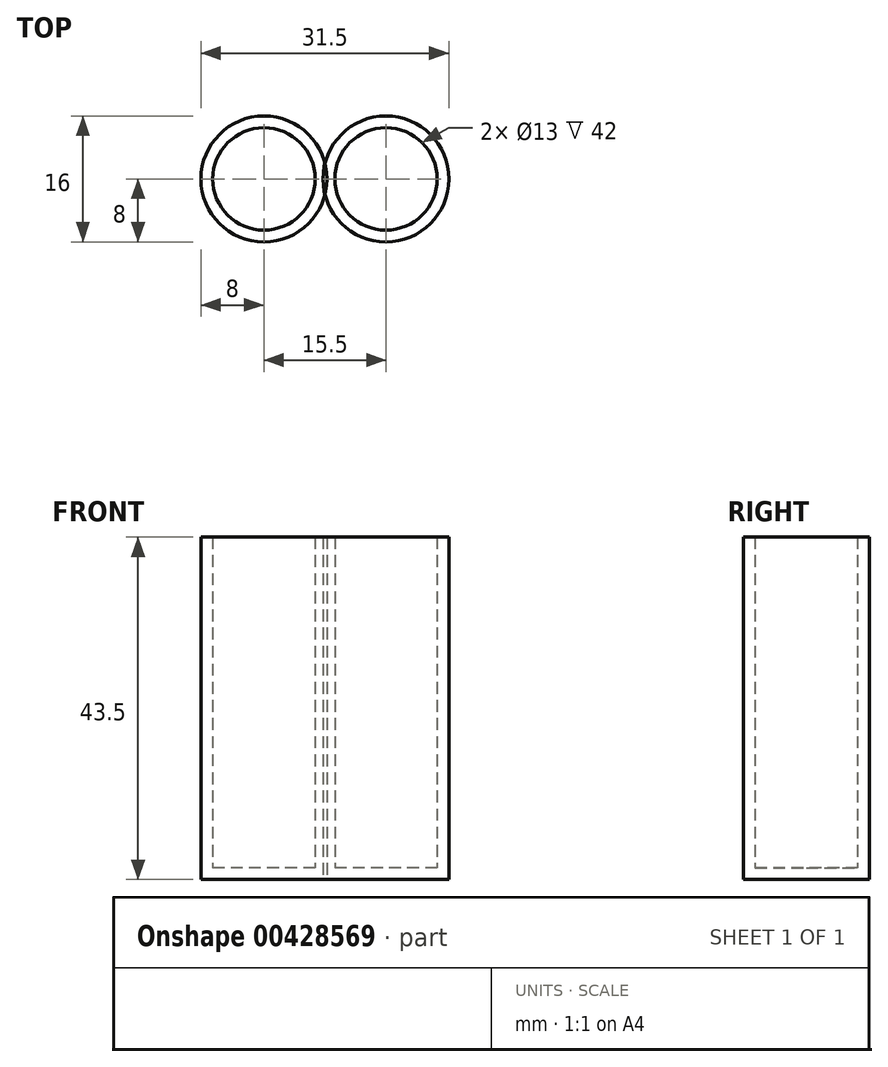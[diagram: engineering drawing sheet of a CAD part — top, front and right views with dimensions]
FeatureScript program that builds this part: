
annotation { "Feature Type Name" : "Feature", "Feature Type Description" : "" }
export const myFeature = defineFeature(function(context is Context, id is Id, definition is map)
    precondition{}
    {
        {
            var Q0;
            Q0=qCreatedBy(makeId("Top.planeOp"),FACE);
            var sketch = newSketch(context, id + "F0", { "sketchPlane" : qUnion([Q0])});
            skCircle(sketch, "E0", {"center": v(0, 0) * mm, "radius": 8 * mm});
            skSolve(sketch);
        }
        {
            var Q0;
            Q0=qSketchRegion(id+"F0",true);
            extrude(context, id + "F1", {"entities" : qUnion([Q0]), "depth" : 43.5 * mm});
        }
        {
            var Q0;
            Q0=makeQuery(id+"F1.opExtrude","CAP_FACE",FACE,{"disambiguationData":[OSD([sQuery(id+"F0.wireOp",EDGE,"E0")])],"isStart":false});
            shell(context, id + "F2", {"entities" : qUnion([Q0]), "thickness" : 1.5 * mm});
        }
        {
            var Q0;
            Q0=makeQuery(id+"F1.opExtrude","SWEPT_BODY",BODY,{"disambiguationData":[OSD([sQuery(id+"F0.wireOp",EDGE,"E0")])]});
            transform(context, id + "F3", {"entities" : qUnion([Q0]), "transformType" : TransformType.TRANSLATION_3D, "dx" : 15.5 * mm, "dy" : 0 * mm, "dz" : 0 * mm, "makeCopy" : true});
        }
    });
